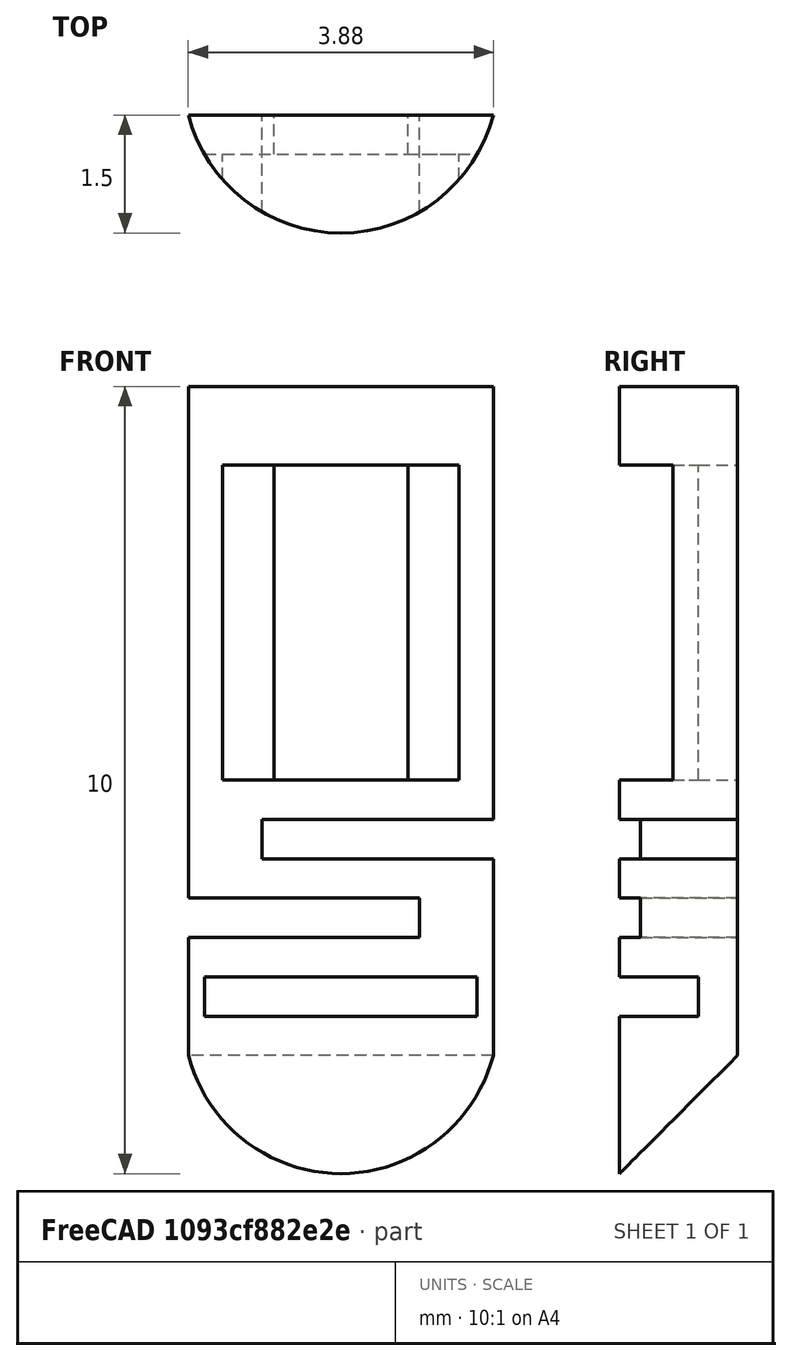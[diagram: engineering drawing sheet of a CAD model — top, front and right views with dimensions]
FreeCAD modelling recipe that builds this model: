
FCSTD DOCUMENT  (FreeCAD 0.19R24267 +99 (Git))
Label: SimpleMirrorMount01
License: All rights reserved
LicenseURL: https://en.wikipedia.org/wiki/All_rights_reserved
objects: Part::Box×7, Part::Cut×4, Part::MultiFuse×2, Part::Cylinder×1
note: 14 computed .brp shape members not serialized (recipe doc carries the construction recipe); baked Part::Feature solids carry a one-line shape summary decoded from their .brp

FEATURE [Part::Cylinder] Cylinder
  Angle = 360
  AttacherType = Attacher::AttachEngine3D
  Height = 10
  Radius = 2
FEATURE [Part::Box] Box  label="Cube"
  AttacherType = Attacher::AttachEngine3D
  Height = 10
  Length = 10
  Placement = pos=(-5,-0.5,0) rot=(0,0,1;0rad)
  Width = 10
FEATURE [Part::Cut] Cut
  Base = -> Cylinder
  Tool = -> Box
FEATURE [Part::Box] Box001  label="Angle Cutter"
  AttacherType = Attacher::AttachEngine3D
  Height = 10
  Length = 10
  Placement = pos=(-5,-7.5,-5.5) rot=(1,0,0;-0.785398rad)
  Width = 10
FEATURE [Part::Box] Box002  label="Cube001"
  AttacherType = Attacher::AttachEngine3D
  Height = 4
  Length = 3
  Placement = pos=(-1.5,-4,4) rot=(0,0,1;0rad)
  Width = 3
FEATURE [Part::Box] Box003  label="Cube002"
  AttacherType = Attacher::AttachEngine3D
  Height = 4
  Length = 1.7
  Placement = pos=(-0.85,-4,4) rot=(0,0,1;0rad)
  Width = 10
FEATURE [Part::MultiFuse] Fusion
  Placement = pos=(0,0,1) rot=(0,0,1;0rad)
  Shapes = -> [Box002,Box003]
FEATURE [Part::Cut] Cut001
  Base = -> Cut
  Tool = -> Fusion
FEATURE [Part::Box] Box004  label="Cube003"
  AttacherType = Attacher::AttachEngine3D
  Height = 0.5
  Length = 10
  Placement = pos=(-1,-5,4) rot=(0,0,1;0rad)
  Width = 10
FEATURE [Part::Box] Box005  label="Cube004"
  AttacherType = Attacher::AttachEngine3D
  Height = 0.5
  Length = 10
  Placement = pos=(-9,-2,3) rot=(0,0,1;0rad)
  Width = 10
FEATURE [Part::Box] Box006  label="Cube005"
  AttacherType = Attacher::AttachEngine3D
  Height = 0.5
  Length = 10
  Placement = pos=(-5,-11,2) rot=(0,0,1;0rad)
  Width = 10
FEATURE [Part::MultiFuse] Fusion001
  Shapes = -> [Box006,Box004,Box005]
FEATURE [Part::Cut] Cut002
  Base = -> Cut001
  Tool = -> Fusion001
FEATURE [Part::Cut] Cut003
  Base = -> Cut002
  Tool = -> Box001
